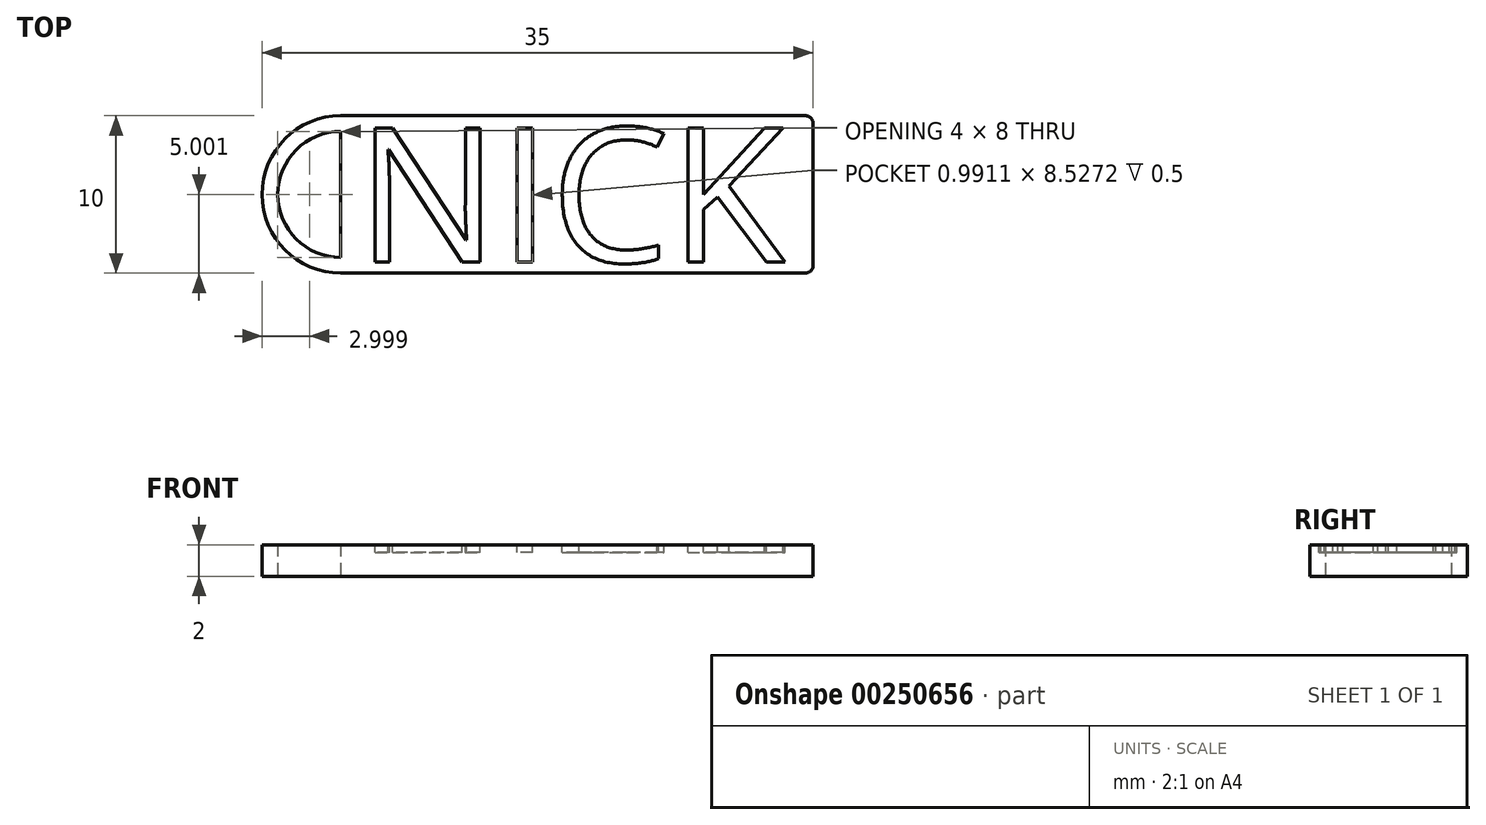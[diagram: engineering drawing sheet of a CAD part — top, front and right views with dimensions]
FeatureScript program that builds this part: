
annotation { "Feature Type Name" : "Feature", "Feature Type Description" : "" }
export const myFeature = defineFeature(function(context is Context, id is Id, definition is map)
    precondition{}
    {
        {
            var Q0;
            Q0=qCreatedBy(makeId("Top.planeOp"),FACE);
            var sketch = newSketch(context, id + "F0", { "sketchPlane" : qUnion([Q0])});
            skLineSegment(sketch, "E0.bottom", {"start": v(-5.27, 3.22) * mm, "end": v(24.73, 3.22) * mm});
            skLineSegment(sketch, "E0.top", {"start": v(-5.27, -6.78) * mm, "end": v(24.73, -6.78) * mm});
            skLineSegment(sketch, "E0.left", {"start": v(-5.27, 3.22) * mm, "end": v(-5.27, -6.78) * mm});
            skLineSegment(sketch, "E0.right", {"start": v(24.73, 3.22) * mm, "end": v(24.73, -6.78) * mm});
            skArc(sketch, "E1", {"start": v(-5.27, 3.22) * mm, "mid": v(-10.27, -1.78) * mm, "end": v(-5.27, -6.78) * mm});
            skArc(sketch, "E2", {"start": v(-5.27, 2.22) * mm, "mid": v(-9.27, -1.78) * mm, "end": v(-5.27, -5.78) * mm});
            skSolve(sketch);
        }
        {
            var Q0;
            Q0=qSketchRegion(id+"F0",true);
            extrude(context, id + "F4", {"entities" : qUnion([Q0]), "depth" : 2 * mm});
        }
        {
            var Q0;
            Q0=makeQuery(id+"F4.opExtrude","SWEPT_EDGE",EDGE,{"disambiguationData":[OSD([sQuery(id+"F0.wireOp",EDGE,"E0.top"),sQuery(id+"F0.wireOp",EDGE,"E0.right")])]});
            var Q1;
            Q1=makeQuery(id+"F4.opExtrude","SWEPT_EDGE",EDGE,{"disambiguationData":[OSD([sQuery(id+"F0.wireOp",EDGE,"E0.bottom"),sQuery(id+"F0.wireOp",EDGE,"E0.right")])]});
            fillet(context, id + "F1", {"entities" : qUnion([Q0, Q1]), "radius" : 0.5 * mm, "tangentPropagation" : true, "allowEdgeOverflow" : false});
        }
        {
            var Q0;
            Q0=makeQuery(id+"F4.opExtrude","CAP_FACE",FACE,{"disambiguationData":[OSD([sQuery(id+"F0.wireOp",EDGE,"E0.bottom"),sQuery(id+"F0.wireOp",EDGE,"E0.top"),sQuery(id+"F0.wireOp",EDGE,"E0.left"),sQuery(id+"F0.wireOp",EDGE,"E0.right"),sQuery(id+"F0.wireOp",EDGE,"E1"),sQuery(id+"F0.wireOp",EDGE,"E2")])],"isStart":false});
            var sketch = newSketch(context, id + "F2", { "sketchPlane" : qUnion([Q0])});
            skText(sketch, "E3", { "text": "NICK", "fontName": "OpenSans-Regular.ttf"});
            skPoint(sketch, "E4", {"position": v(-4.27, -1.78) * mm});
            skPoint(sketch, "E5", {"position": v(23.73, -1.78) * mm});
            skPoint(sketch, "E6", {"position": v(-5.27, -1.78) * mm});
            skPoint(sketch, "E7", {"position": v(24.73, -1.78) * mm});
            const initialGuessF2  = {"E3": [-0.00427, -0.00608, 1, 0, 0.0086]};
            skSetInitialGuess(sketch, initialGuessF2);
            skSolve(sketch);
        }
        {
            var Q0;
            Q0 = qSketchRegion(id + "F2", true);
            extrude(context, id + "F3", {"entities" : qUnion([Q0]), "operationType" : NewBodyOperationType.REMOVE, "oppositeDirection" : true, "depth" : 0.5 * mm});
        }
    });
